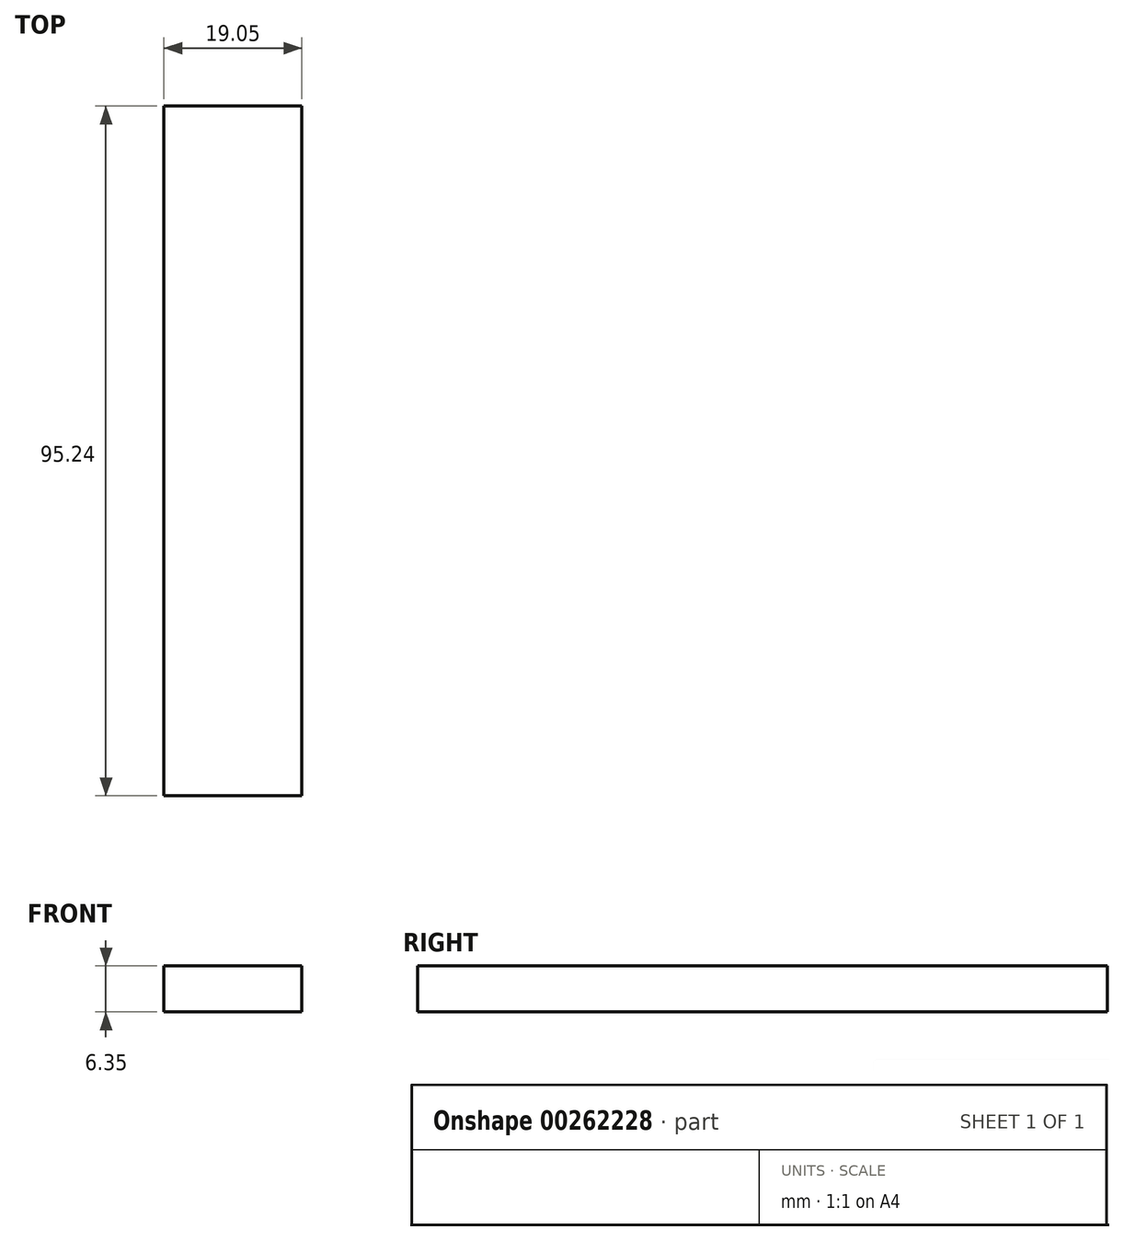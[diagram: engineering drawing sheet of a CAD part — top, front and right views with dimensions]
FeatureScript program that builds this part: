
annotation { "Feature Type Name" : "Feature", "Feature Type Description" : "" }
export const myFeature = defineFeature(function(context is Context, id is Id, definition is map)
    precondition{}
    {
        {
            var Q0;
            Q0=qCreatedBy(makeId("Front.planeOp"),FACE);
            var sketch = newSketch(context, id + "F0", { "sketchPlane" : qUnion([Q0])});
            skLineSegment(sketch, "E0.bottom", {"start": v(-6.77, 1.22) * mm, "end": v(12.28, 1.22) * mm});
            skLineSegment(sketch, "E0.top", {"start": v(-6.77, -5.13) * mm, "end": v(12.28, -5.13) * mm});
            skLineSegment(sketch, "E0.left", {"start": v(-6.77, 1.22) * mm, "end": v(-6.77, -5.13) * mm});
            skLineSegment(sketch, "E0.right", {"start": v(12.28, 1.22) * mm, "end": v(12.28, -5.13) * mm});
            skSolve(sketch);
        }
        {
            var Q0;
            Q0 = qSketchRegion(id + "F0", true);
            extrude(context, id + "F1", {"entities" : qUnion([Q0]), "endBound" : BoundingType.SYMMETRIC, "depth" : 95.25 * mm});
        }
    });
